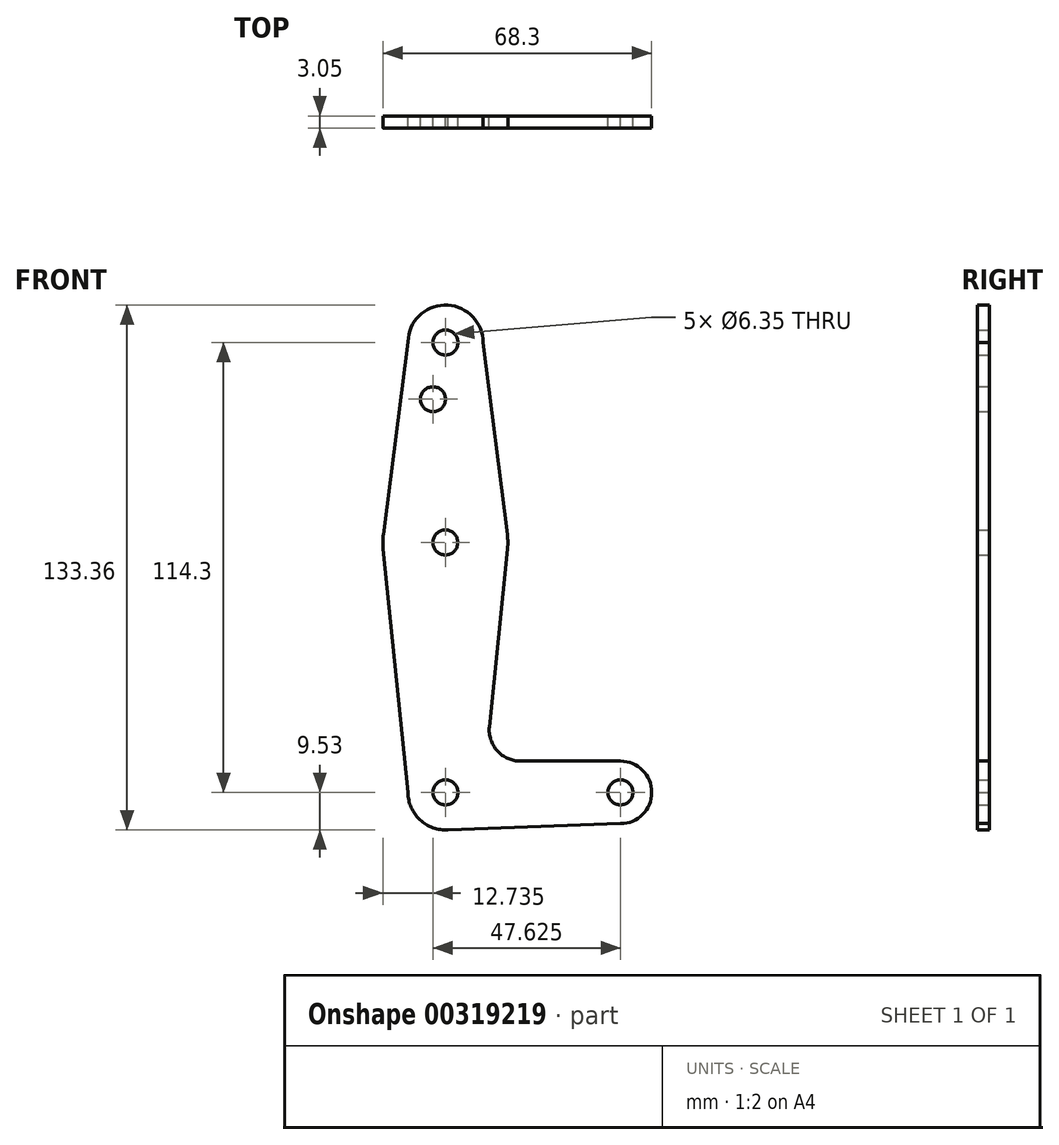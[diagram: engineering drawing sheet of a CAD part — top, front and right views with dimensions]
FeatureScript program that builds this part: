
annotation { "Feature Type Name" : "Feature", "Feature Type Description" : "" }
export const myFeature = defineFeature(function(context is Context, id is Id, definition is map)
    precondition{}
    {
        {
            var Q0;
            Q0=qCreatedBy(makeId("Front.planeOp"),FACE);
            var sketch = newSketch(context, id + "F0", { "sketchPlane" : qUnion([Q0])});
            skLineSegment(sketch, "E0", {"start": v(0, 0) * mm, "end": v(0, 114.3) * mm, "construction": true});
            skLineSegment(sketch, "E1", {"start": v(44.45, 0) * mm, "end": v(0, 0) * mm, "construction": true});
            skCircle(sketch, "E2", {"center": v(-0.04, 63.5) * mm, "radius": 15.88 * mm});
            skCircle(sketch, "E3", {"center": v(0, 0) * mm, "radius": 9.53 * mm});
            skCircle(sketch, "E4", {"center": v(44.45, 0) * mm, "radius": 7.94 * mm});
            skCircle(sketch, "E5", {"center": v(0, 114.3) * mm, "radius": 9.53 * mm});
            skLineSegment(sketch, "E6", {"start": v(19.06, 7.94) * mm, "end": v(44.45, 7.94) * mm});
            skLineSegment(sketch, "E7", {"start": v(0, -9.53) * mm, "end": v(44.45, -7.94) * mm});
            skLineSegment(sketch, "E8", {"start": v(-9.52, 0) * mm, "end": v(-15.83, 61.9) * mm});
            skLineSegment(sketch, "E9", {"start": v(11.15, 16.7) * mm, "end": v(15.76, 61.9) * mm});
            skLineSegment(sketch, "E10", {"start": v(-9.45, 115.5) * mm, "end": v(-15.79, 65.5) * mm});
            skLineSegment(sketch, "E11", {"start": v(9.52, 114.3) * mm, "end": v(15.71, 65.5) * mm});
            skCircle(sketch, "E12", {"center": v(0, 114.3) * mm, "radius": 3.18 * mm});
            skCircle(sketch, "E13", {"center": v(-0.04, 63.5) * mm, "radius": 3.18 * mm});
            skCircle(sketch, "E14", {"center": v(0, 0) * mm, "radius": 3.18 * mm});
            skArc(sketch, "E15.filletArc", {"start": v(11.15, 16.7) * mm, "mid": v(13.16, 10.56) * mm, "end": v(19.06, 7.94) * mm});
            skCircle(sketch, "E16", {"center": v(-3.18, 99.9) * mm, "radius": 3.18 * mm});
            skCircle(sketch, "E17", {"center": v(44.45, 0) * mm, "radius": 3.18 * mm});
            skSolve(sketch);
        }
        {
            var Q0;
            Q0 = qSketchRegion(id + "F0", true);
            extrude(context, id + "F1", {"entities" : qUnion([Q0]), "depth" : 3.05 * mm});
        }
    });
